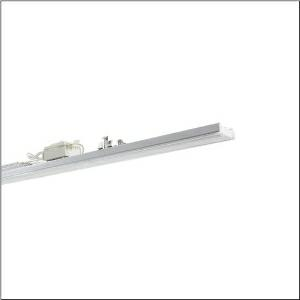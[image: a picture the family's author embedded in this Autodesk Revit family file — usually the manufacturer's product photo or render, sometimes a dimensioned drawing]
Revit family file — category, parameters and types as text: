
# Revit family: licross_r__21_recessed_mo_52te12dv4fxg_0884
name_source: partatom
category: Lighting Fixtures
units: mm (PartAtom-declared; Revit-internal decimal feet)

## family parameters
Cut with Voids When Loaded = No
Host = Face
Light Source = No
Part Type = Normal
Room Calculation Point = No
Round Connector Dimension = Use Diameter
Shared = No

## types (1)
- --- (1 x LED, 15420 lm, 85.3 W, 4000K)
    Apparent Load = 85 VA
    CIE Flux Codes = 72 92 99 100 100
    Color Rendering = 80
    Color Temperature = 4000K
    Default Elevation = 1800 mm
    Description = Licross® 21 Recessed MO, luminaire insert, of sheet steel, galvanised, coil coated, white, length: 2.250mm, width: 66mm, height: 67mm, LED rated luminous flux: 15.420lm, light colour: 840, control gear: DALI 2, with plug, 5-pole, with phase selection, mains connection: 220..240V, AC, 50/60Hz, rated input power: 85W, halogen-free wiring, primary optical cover: cover, of PMMA, light emission: direct distribution, primary light characteristic: symmetric, protection rating (complete): IP54, insulation class (complete): insulation class I (protective earthing), certification: CE, ENEC, VDE, UKCA, protection symbol: D if used in an environment with non-conductive dust loads with corresponding accessories, impact resistance: IK06, permissible ambient temperature for indoor applications: -25..+35°C, corresponds to IFS (International Featured Standards) requirements for safety and quality in the food industry, reducing of maximum allowable ambient temperature of 5°C with ceiling mounting, LABS conformity tested according to VDMA 24364:2018-05, packaging unit: 1 piece
    Height = 58 mm
    Lamp = 1 x LED
    Lamp Light Flux = 15420 lm
    Lamp Power = 85.3 W
    Lamp count = 1
    Length = 2250 mm
    Luminous efficacy = 181 lm/W
    Manufacturer = Siteco
    ModVariant = No
    Model = 52TE12DV4FXG
    Mounting Place = Ceiling
    Mounting Type = Pendant
    Number of Poles = 1
    OnlyDefault = Yes
    Power Factor = 1
    Product Name = Licross® 21 Recessed MO
    Product group = luminaire insert
    ProductGroupID = 902
    Protection Class = Protection class I
    Protection Degree = IP 54
    RLX_Detail_Level = 1
    RLX_Emergency_Light_Flux = 0 lm
    RLX_Emergency_Type = 0
    RLX_Emergency_Type_DB = No
    RlxData = <blob elided: 29481 chars, md5=d013fd39>
    Socket = socket
    Standby Power = 0 W
    System Light Flux = 15420 lm
    System Power = 85 W
    Type Comments = factory setting: luminous flux: 100 % | dim-lin: 254 | 390 mA
    Type Image = l_1296930.jpg
    URL = http://relux.com
    VarID = @adj_126412
    Voltage = 0 V
    Weight = 0.00 kg
    Width = 66 mm

## geometry (parser evidence)
native form markers: Blend x4, Sweep x10
no freeform markers — native parametric forms only
